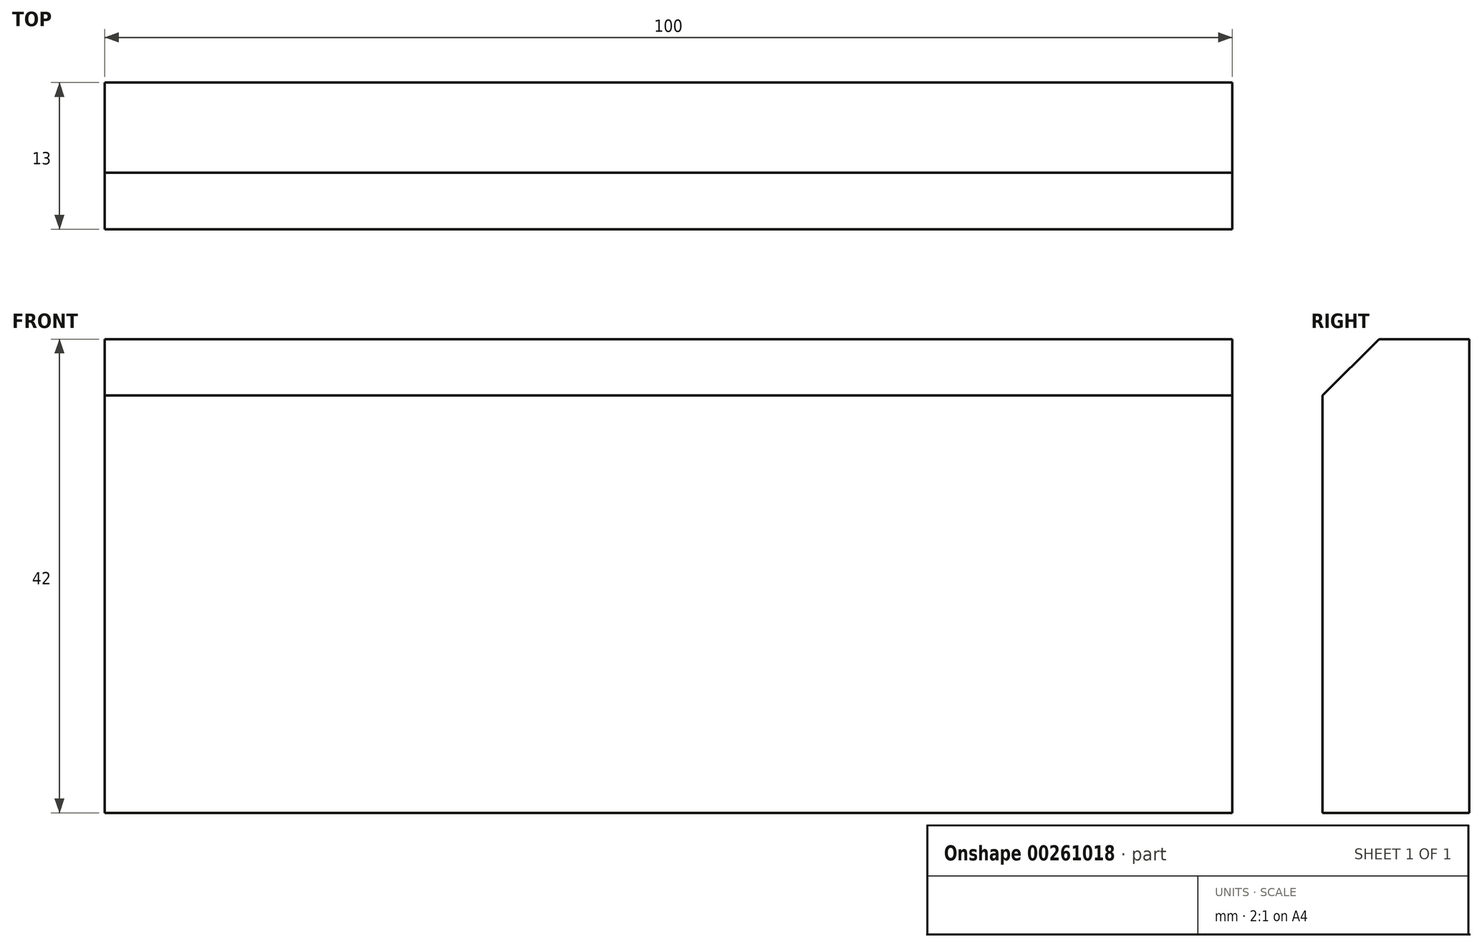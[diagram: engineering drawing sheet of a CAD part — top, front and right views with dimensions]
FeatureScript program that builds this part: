
annotation { "Feature Type Name" : "Feature", "Feature Type Description" : "" }
export const myFeature = defineFeature(function(context is Context, id is Id, definition is map)
    precondition{}
    {
        {
            var Q0;
            Q0=qCreatedBy(makeId("Front.planeOp"),FACE);
            var sketch = newSketch(context, id + "F0", { "sketchPlane" : qUnion([Q0])});
            skLineSegment(sketch, "E0.bottom", {"start": v(-51.07, 22.61) * mm, "end": v(48.93, 22.61) * mm});
            skLineSegment(sketch, "E0.top", {"start": v(-51.07, -19.39) * mm, "end": v(48.93, -19.39) * mm});
            skLineSegment(sketch, "E0.left", {"start": v(-51.07, 22.61) * mm, "end": v(-51.07, -19.39) * mm});
            skLineSegment(sketch, "E0.right", {"start": v(48.93, 22.61) * mm, "end": v(48.93, -19.39) * mm});
            skSolve(sketch);
        }
        {
            var Q0;
            Q0 = qSketchRegion(id + "F0", true);
            extrude(context, id + "F1", {"entities" : qUnion([Q0]), "depth" : 13 * mm});
        }
        {
            var Q0;
            Q0=makeQuery(id+"F1.opExtrude","CAP_EDGE",EDGE,{"disambiguationData":[OSD([sQuery(id+"F0.wireOp",EDGE,"E0.bottom")])],"isStart":false});
            chamfer(context, id + "F2", {"entities" : qUnion([Q0]), "width" : 5 * mm, "tangentPropagation" : true});
        }
    });
